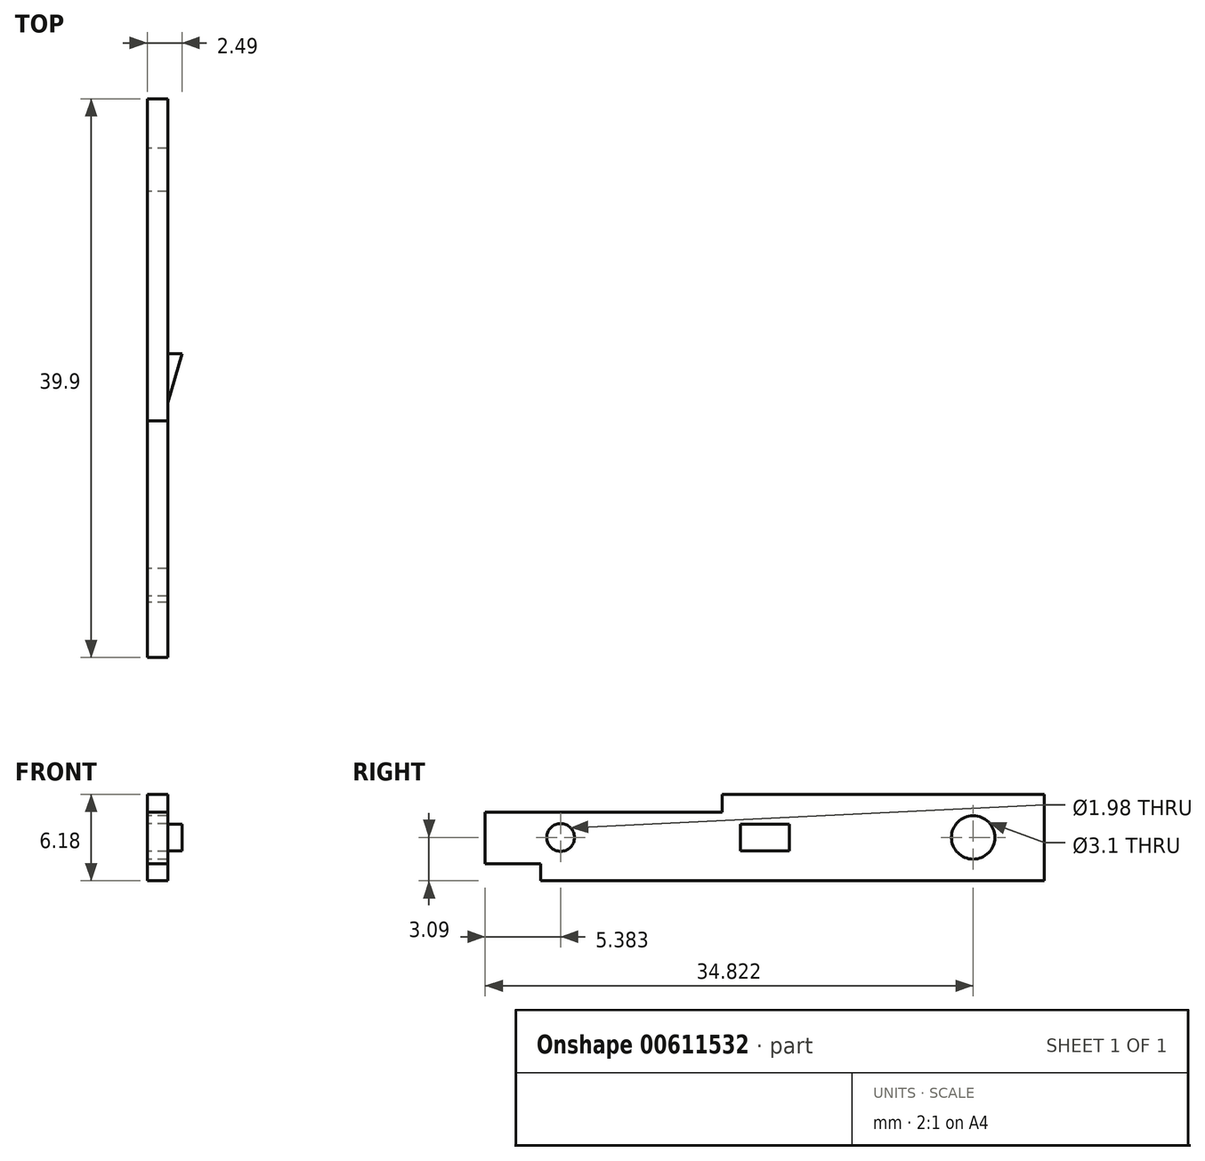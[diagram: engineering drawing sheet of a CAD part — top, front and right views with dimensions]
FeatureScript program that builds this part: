
annotation { "Feature Type Name" : "Feature", "Feature Type Description" : "" }
export const myFeature = defineFeature(function(context is Context, id is Id, definition is map)
    precondition{}
    {
        {
            var Q0;
            Q0=qCreatedBy(makeId("Right.planeOp"),FACE);
            var sketch = newSketch(context, id + "F0", { "sketchPlane" : qUnion([Q0])});
            skLineSegment(sketch, "E0.bottom", {"start": v(-19.95, 3.09) * mm, "end": v(19.95, 3.09) * mm});
            skLineSegment(sketch, "E0.top", {"start": v(-19.95, -3.09) * mm, "end": v(19.95, -3.09) * mm});
            skLineSegment(sketch, "E0.left", {"start": v(-19.95, 3.09) * mm, "end": v(-19.95, -3.09) * mm});
            skLineSegment(sketch, "E0.right", {"start": v(19.95, 3.09) * mm, "end": v(19.95, -3.09) * mm});
            skCircle(sketch, "E1", {"center": v(-14.57, 0) * mm, "radius": 1 * mm});
            skCircle(sketch, "E2", {"center": v(14.87, 0) * mm, "radius": 1.55 * mm});
            skLineSegment(sketch, "E3.top", {"start": v(-19.95, -1.9) * mm, "end": v(-15.99, -1.9) * mm});
            skLineSegment(sketch, "E3.right", {"start": v(-15.99, -3.09) * mm, "end": v(-15.99, -1.9) * mm});
            skLineSegment(sketch, "E4.top", {"start": v(-19.95, 1.82) * mm, "end": v(-3.04, 1.82) * mm});
            skLineSegment(sketch, "E4.right", {"start": v(-3.04, 3.09) * mm, "end": v(-3.04, 1.82) * mm});
            skSolve(sketch);
        }
        {
            var Q0;
            {var subQ0=sQuery(id+"F0.wireOp",EDGE,"E0.right");Q0=makeQuery(id+"F0.imprint","IMPRINT",FACE,{"disambiguationData":[TD([[makeQuery(id+"F0.imprint","IMPRINT",EDGE,{"derivedFrom":subQ0}),-1.0]])]});}
            extrude(context, id + "F1", {"entities" : qUnion([Q0]), "endBound" : BoundingType.SYMMETRIC, "depth" : 1.47 * mm, "offsetDistance" : 25.4 * mm});
        }
        {
            var Q0;
            Q0=makeQuery(id+"F1.opExtrude","CAP_FACE",FACE,{"disambiguationData":[OSD([sQuery(id+"F0.wireOp",EDGE,"E0.bottom"),sQuery(id+"F0.wireOp",EDGE,"E0.top"),sQuery(id+"F0.wireOp",EDGE,"E0.left"),sQuery(id+"F0.wireOp",EDGE,"E0.right"),sQuery(id+"F0.wireOp",EDGE,"E1"),sQuery(id+"F0.wireOp",EDGE,"E2"),sQuery(id+"F0.wireOp",EDGE,"E3.top"),sQuery(id+"F0.wireOp",EDGE,"E3.right"),sQuery(id+"F0.wireOp",EDGE,"E4.top"),sQuery(id+"F0.wireOp",EDGE,"E4.right")])],"isStart":false});
            var sketch = newSketch(context, id + "F2", { "sketchPlane" : qUnion([Q0])});
            skLineSegment(sketch, "E5.bottom", {"start": v(-1.75, 0.95) * mm, "end": v(1.74, 0.95) * mm});
            skLineSegment(sketch, "E5.top", {"start": v(-1.75, -0.95) * mm, "end": v(1.74, -0.95) * mm});
            skLineSegment(sketch, "E5.left", {"start": v(-1.75, 0.95) * mm, "end": v(-1.75, -0.95) * mm});
            skLineSegment(sketch, "E5.right", {"start": v(1.74, 0.95) * mm, "end": v(1.74, -0.95) * mm});
            skSolve(sketch);
        }
        {
            var Q0;
            Q0=makeQuery(id+"F2.imprint","IMPRINT",FACE,{"disambiguationData":[TD([[makeQuery(id+"F2.imprint","IMPRINT",EDGE,{"derivedFrom":sQuery(id+"F2.wireOp",EDGE,"E5.bottom")}),-1.0]])]});
            extrude(context, id + "F3", {"entities" : qUnion([Q0]), "operationType" : NewBodyOperationType.ADD, "depth" : 1.02 * mm, "offsetDistance" : 25.4 * mm});
        }
        {
            var Q0;
            Q0=makeQuery(id+"F3.opExtrude","SWEPT_FACE",FACE,{"disambiguationData":[OSD([sQuery(id+"F2.wireOp",EDGE,"E5.top")])]});
            var sketch = newSketch(context, id + "F4", { "sketchPlane" : qUnion([Q0])});
            skLineSegment(sketch, "E6", {"start": v(0.74, 1.75) * mm, "end": v(1.75, -1.74) * mm});
            skLineSegment(sketch, "E7", {"start": v(1.75, -1.74) * mm, "end": v(1.75, 1.75) * mm});
            skLineSegment(sketch, "E8", {"start": v(1.75, 1.75) * mm, "end": v(0.74, 1.75) * mm});
            skSolve(sketch);
        }
        {
            var Q0;
            Q0=makeQuery(id+"F4.imprint","IMPRINT",FACE,{"disambiguationData":[TD([[makeQuery(id+"F4.imprint","IMPRINT",EDGE,{"derivedFrom":sQuery(id+"F4.wireOp",EDGE,"E6")}),1.0]])]});
            extrude(context, id + "F5", {"entities" : qUnion([Q0]), "operationType" : NewBodyOperationType.REMOVE, "oppositeDirection" : true, "depth" : 25.4 * mm, "offsetDistance" : 25.4 * mm});
        }
    });
